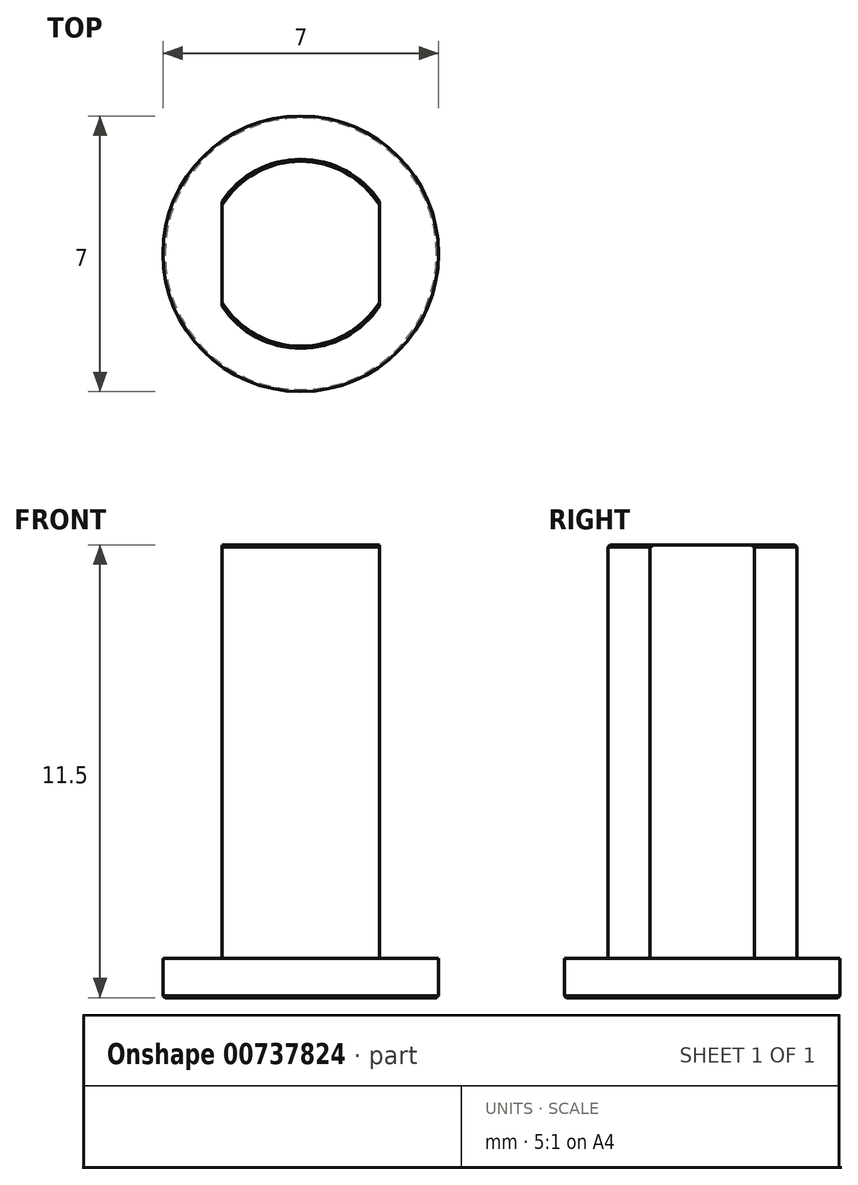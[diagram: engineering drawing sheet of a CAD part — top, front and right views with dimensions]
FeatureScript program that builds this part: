
annotation { "Feature Type Name" : "Feature", "Feature Type Description" : "" }
export const myFeature = defineFeature(function(context is Context, id is Id, definition is map)
    precondition{}
    {
        {
            var Q0;
            Q0=qCreatedBy(makeId("Top.planeOp"),FACE);
            var sketch = newSketch(context, id + "F0", { "sketchPlane" : qUnion([Q0])});
            skCircle(sketch, "E0", {"center": v(0, 0) * mm, "radius": 2.4 * mm});
            skLineSegment(sketch, "E1", {"start": v(-2, 1.33) * mm, "end": v(2, 1.33) * mm});
            skLineSegment(sketch, "E2", {"start": v(-2, -1.33) * mm, "end": v(2, -1.33) * mm});
            skLineSegment(sketch, "E3", {"start": v(-2, 1.33) * mm, "end": v(-2, -1.33) * mm});
            skLineSegment(sketch, "E4", {"start": v(2, 1.33) * mm, "end": v(2, -1.33) * mm});
            skCircle(sketch, "E5", {"center": v(0, 0) * mm, "radius": 3.5 * mm});
            skSolve(sketch);
        }
        {
            var Q0;
            {var subQ0=sQuery(id+"F0.wireOp",EDGE,"E1");Q0=makeQuery(id+"F0.imprint","IMPRINT",FACE,{"disambiguationData":[TD([[makeQuery(id+"F0.imprint","IMPRINT",EDGE,{"derivedFrom":subQ0}),1.0]])]});}
            var Q1;
            Q1=makeQuery(id+"F0.imprint","IMPRINT",FACE,{"disambiguationData":[TD([[makeQuery(id+"F0.imprint","IMPRINT",EDGE,{"derivedFrom":sQuery(id+"F0.wireOp",EDGE,"E1")}),-1.0]])]});
            var Q2;
            {var subQ0=sQuery(id+"F0.wireOp",EDGE,"E2");Q2=makeQuery(id+"F0.imprint","IMPRINT",FACE,{"disambiguationData":[TD([[makeQuery(id+"F0.imprint","IMPRINT",EDGE,{"derivedFrom":subQ0}),-1.0]])]});}
            extrude(context, id + "F1", {"entities" : qUnion([Q0, Q1, Q2]), "depth" : 11.5 * mm, "offsetDistance" : 25 * mm});
        }
        {
            var Q0;
            Q0=makeQuery(id+"F0.imprint","IMPRINT",FACE,{"disambiguationData":[TD([[makeQuery(id+"F0.imprint","IMPRINT",EDGE,{"derivedFrom":sQuery(id+"F0.wireOp",EDGE,"E5")}),1.0]])]});
            var Q1;
            {var subQ0=sQuery(id+"F0.wireOp",EDGE,"E4");Q1=makeQuery(id+"F0.imprint","IMPRINT",FACE,{"disambiguationData":[TD([[makeQuery(id+"F0.imprint","IMPRINT",EDGE,{"derivedFrom":subQ0}),1.0]])]});}
            var Q2;
            {var subQ0=sQuery(id+"F0.wireOp",EDGE,"E3");Q2=makeQuery(id+"F0.imprint","IMPRINT",FACE,{"disambiguationData":[TD([[makeQuery(id+"F0.imprint","IMPRINT",EDGE,{"derivedFrom":subQ0}),-1.0]])]});}
            extrude(context, id + "F2", {"entities" : qUnion([Q0, Q1, Q2]), "operationType" : NewBodyOperationType.ADD, "depth" : 1 * mm, "offsetDistance" : 25 * mm});
        }
        {
            var Q0;
            {var subQ0=sQuery(id+"F0.wireOp",EDGE,"E2");var subQ1=sQuery(id+"F0.wireOp",EDGE,"E0");Q0=makeQuery(id+"F1.opExtrude","CAP_EDGE",EDGE,{"disambiguationData":[OSD([subQ1]),TDD([makeQuery(id+"F0.imprint","IMPRINT",EDGE,{"disambiguationData":[TD([[makeQuery(id+"F0.imprint","INTERSECT",VERTEX,{"derivedFrom":[subQ1,subQ0,sQuery(id+"F0.wireOp",EDGE,"E3")]}),-1.0]])],"derivedFrom":subQ1})])],"isStart":false});}
            var Q1;
            {var subQ0=sQuery(id+"F0.wireOp",EDGE,"E1");var subQ1=sQuery(id+"F0.wireOp",EDGE,"E0");Q1=makeQuery(id+"F1.opExtrude","CAP_EDGE",EDGE,{"disambiguationData":[OSD([subQ1]),TDD([makeQuery(id+"F0.imprint","IMPRINT",EDGE,{"disambiguationData":[TD([[makeQuery(id+"F0.imprint","INTERSECT",VERTEX,{"derivedFrom":[subQ1,subQ0,sQuery(id+"F0.wireOp",EDGE,"E3")]}),1.0]])],"derivedFrom":subQ1})])],"isStart":false});}
            chamfer(context, id + "F3", {"entities" : qUnion([Q0, Q1]), "width" : 0.05 * mm, "tangentPropagation" : true});
        }
        {
            var Q0;
            Q0=makeQuery(id+"F2.opExtrude","CAP_EDGE",EDGE,{"disambiguationData":[OSD([sQuery(id+"F0.wireOp",EDGE,"E5")])],"isStart":true});
            chamfer(context, id + "F4", {"entities" : qUnion([Q0]), "width" : 0.05 * mm, "tangentPropagation" : true});
        }
    });
